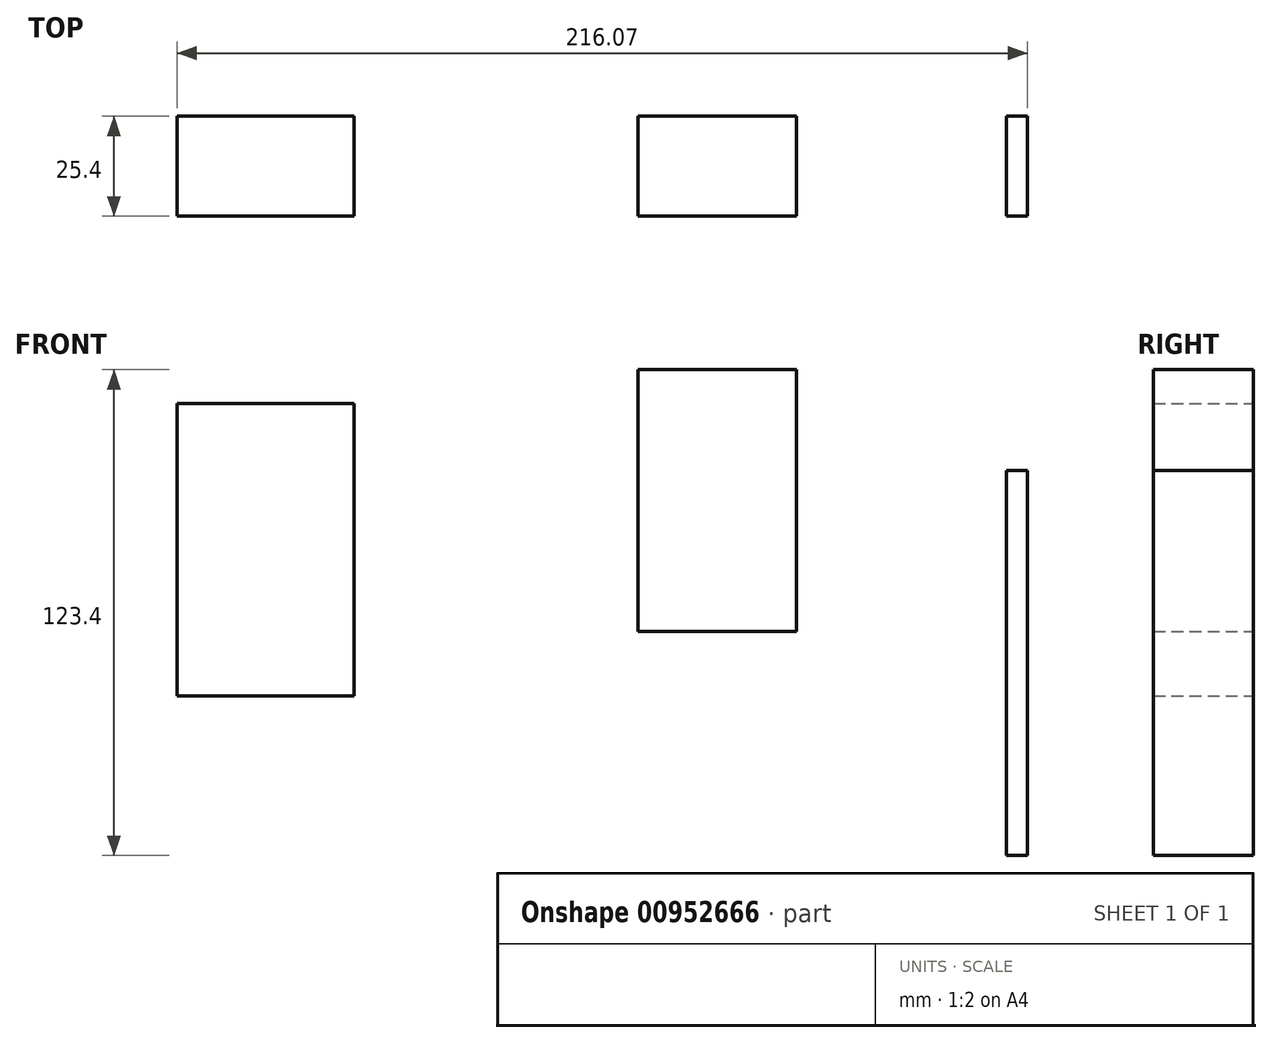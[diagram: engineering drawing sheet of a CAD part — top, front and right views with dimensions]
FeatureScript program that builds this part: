
annotation { "Feature Type Name" : "Feature", "Feature Type Description" : "" }
export const myFeature = defineFeature(function(context is Context, id is Id, definition is map)
    precondition{}
    {
        {
            var Q0;
            Q0=qCreatedBy(makeId("Front.planeOp"),FACE);
            var sketch = newSketch(context, id + "F0", { "sketchPlane" : qUnion([Q0])});
            skLineSegment(sketch, "E0.bottom", {"start": v(-33.78, 0) * mm, "end": v(-78.81, 0) * mm});
            skLineSegment(sketch, "E0.top", {"start": v(-33.78, 74.34) * mm, "end": v(-78.81, 74.34) * mm});
            skLineSegment(sketch, "E0.left", {"start": v(-33.78, 0) * mm, "end": v(-33.78, 74.34) * mm});
            skLineSegment(sketch, "E0.right", {"start": v(-78.81, 0) * mm, "end": v(-78.81, 74.34) * mm});
            skPoint(sketch, "E0.middle", {"position": v(-56.3, 37.17) * mm});
            skLineSegment(sketch, "E1.bottom", {"start": v(78.57, 16.45) * mm, "end": v(38.33, 16.45) * mm});
            skLineSegment(sketch, "E1.top", {"start": v(78.57, 82.93) * mm, "end": v(38.33, 82.93) * mm});
            skLineSegment(sketch, "E1.left", {"start": v(78.57, 16.45) * mm, "end": v(78.57, 82.93) * mm});
            skLineSegment(sketch, "E1.right", {"start": v(38.33, 16.45) * mm, "end": v(38.33, 82.93) * mm});
            skPoint(sketch, "E1.middle", {"position": v(58.45, 49.7) * mm});
            skLineSegment(sketch, "E2.bottom", {"start": v(132, -40.47) * mm, "end": v(137.26, -40.47) * mm});
            skLineSegment(sketch, "E2.top", {"start": v(132, 57.35) * mm, "end": v(137.26, 57.35) * mm});
            skLineSegment(sketch, "E2.left", {"start": v(132, -40.47) * mm, "end": v(132, 57.35) * mm});
            skLineSegment(sketch, "E2.right", {"start": v(137.26, -40.47) * mm, "end": v(137.26, 57.35) * mm});
            skPoint(sketch, "E2.middle", {"position": v(134.63, 8.44) * mm});
            skSolve(sketch);
        }
        {
            var Q0;
            Q0=makeQuery(id+"F0.imprint","IMPRINT",FACE,{"disambiguationData":[TD([[makeQuery(id+"F0.imprint","IMPRINT",EDGE,{"derivedFrom":sQuery(id+"F0.wireOp",EDGE,"E0.bottom")}),-1.0]])]});
            var Q1;
            Q1=makeQuery(id+"F0.imprint","IMPRINT",FACE,{"disambiguationData":[TD([[makeQuery(id+"F0.imprint","IMPRINT",EDGE,{"derivedFrom":sQuery(id+"F0.wireOp",EDGE,"E1.bottom")}),-1.0]])]});
            var Q2;
            Q2=makeQuery(id+"F0.imprint","IMPRINT",FACE,{"disambiguationData":[TD([[makeQuery(id+"F0.imprint","IMPRINT",EDGE,{"derivedFrom":sQuery(id+"F0.wireOp",EDGE,"E2.bottom")}),1.0]])]});
            var Q3;
            Q3 = qSketchRegion(id + "F0", true);
            extrude(context, id + "F1", {"entities" : qUnion([Q0, Q1, Q2, Q3]), "depth" : 25.4 * mm, "offsetDistance" : 25.4 * mm});
        }
    });
